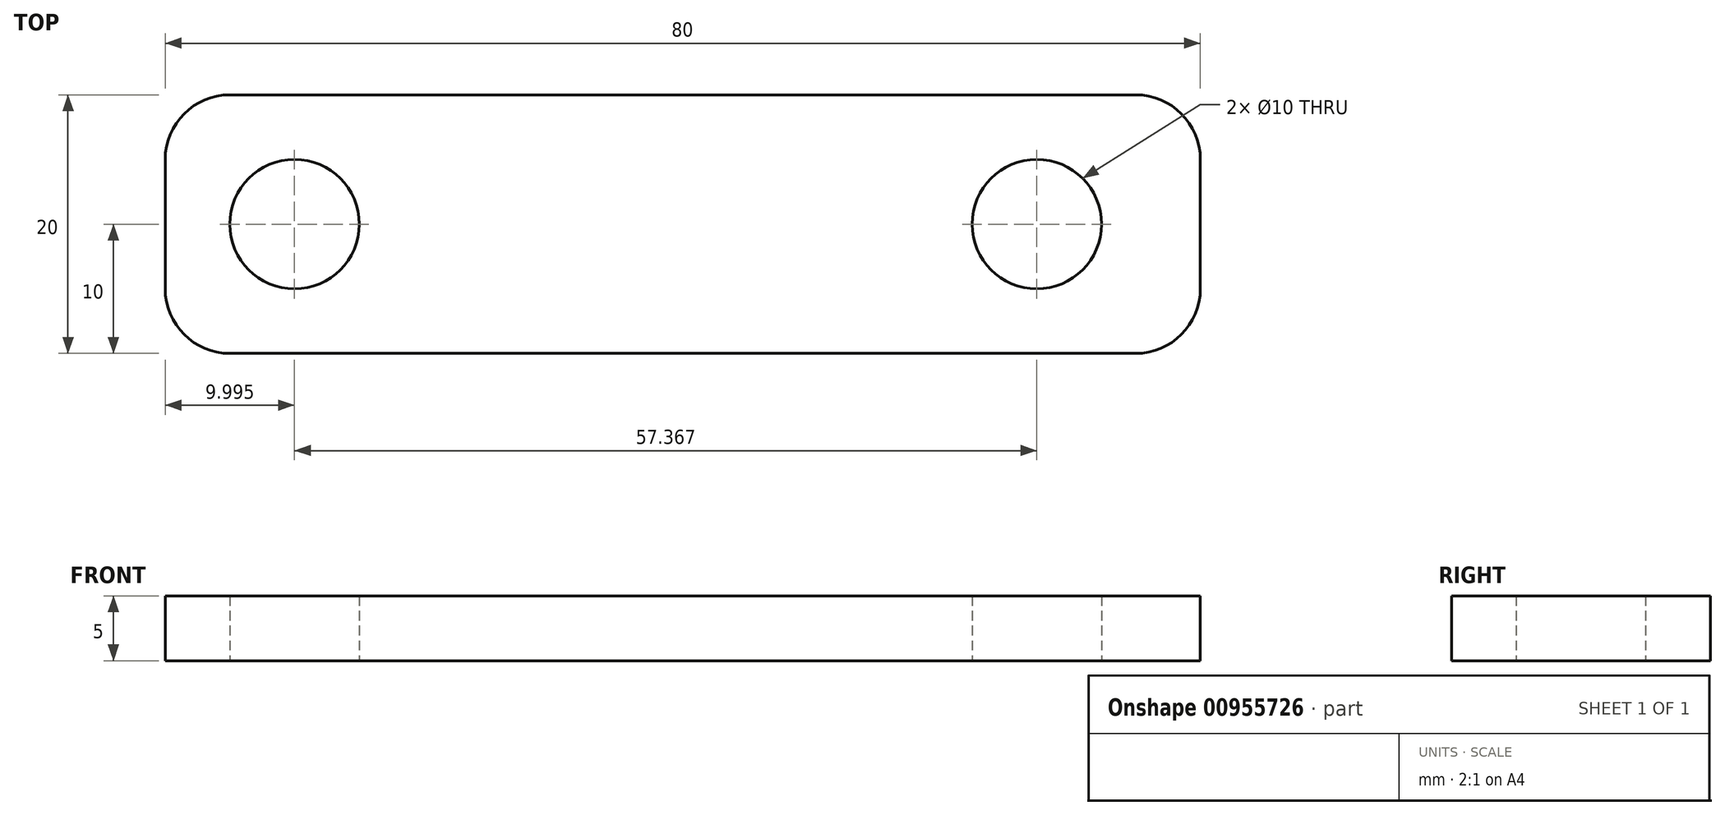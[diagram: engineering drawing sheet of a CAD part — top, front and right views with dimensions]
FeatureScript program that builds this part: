
annotation { "Feature Type Name" : "Feature", "Feature Type Description" : "" }
export const myFeature = defineFeature(function(context is Context, id is Id, definition is map)
    precondition{}
    {
        {
            var Q0;
            Q0=qCreatedBy(makeId("Top.planeOp"),FACE);
            var sketch = newSketch(context, id + "F0", { "sketchPlane" : qUnion([Q0])});
            skLineSegment(sketch, "E0.bottom", {"start": v(40, 10) * mm, "end": v(-40, 10) * mm});
            skLineSegment(sketch, "E0.top", {"start": v(40, -10) * mm, "end": v(-40, -10) * mm});
            skLineSegment(sketch, "E0.left", {"start": v(40, 10) * mm, "end": v(40, -10) * mm});
            skLineSegment(sketch, "E0.right", {"start": v(-40, 10) * mm, "end": v(-40, -10) * mm});
            skPoint(sketch, "E0.middle", {"position": v(0, 0) * mm});
            skSolve(sketch);
        }
        {
            var Q0;
            Q0=makeQuery(id+"F0.imprint","IMPRINT",FACE,{"disambiguationData":[TD([[makeQuery(id+"F0.imprint","IMPRINT",EDGE,{"derivedFrom":sQuery(id+"F0.wireOp",EDGE,"E0.bottom")}),1.0]])]});
            extrude(context, id + "F1", {"entities" : qUnion([Q0]), "depth" : 5 * mm, "offsetDistance" : 25 * mm});
        }
        {
            var Q0;
            Q0=qCreatedBy(makeId("Top.planeOp"),FACE);
            var sketch = newSketch(context, id + "F2", { "sketchPlane" : qUnion([Q0])});
            skCircle(sketch, "E1", {"center": v(-30, 0) * mm, "radius": 5 * mm});
            skCircle(sketch, "E2", {"center": v(27.36, 0) * mm, "radius": 5 * mm});
            skSolve(sketch);
        }
        {
            var Q0;
            Q0 = qSketchRegion(id + "F2", true);
            extrude(context, id + "F3", {"entities" : qUnion([Q0]), "operationType" : NewBodyOperationType.REMOVE, "endBound" : BoundingType.THROUGH_ALL, "depth" : 25 * mm, "offsetDistance" : 25 * mm});
        }
        {
            var Q0;
            Q0=makeQuery(id+"F1.opExtrude","SWEPT_EDGE",EDGE,{"disambiguationData":[OSD([sQuery(id+"F0.wireOp",EDGE,"E0.top"),sQuery(id+"F0.wireOp",EDGE,"E0.left")])]});
            var Q1;
            Q1=makeQuery(id+"F1.opExtrude","SWEPT_EDGE",EDGE,{"disambiguationData":[OSD([sQuery(id+"F0.wireOp",EDGE,"E0.bottom"),sQuery(id+"F0.wireOp",EDGE,"E0.left")])]});
            var Q2;
            Q2=makeQuery(id+"F1.opExtrude","SWEPT_EDGE",EDGE,{"disambiguationData":[OSD([sQuery(id+"F0.wireOp",EDGE,"E0.top"),sQuery(id+"F0.wireOp",EDGE,"E0.right")])]});
            var Q3;
            Q3=makeQuery(id+"F1.opExtrude","SWEPT_EDGE",EDGE,{"disambiguationData":[OSD([sQuery(id+"F0.wireOp",EDGE,"E0.bottom"),sQuery(id+"F0.wireOp",EDGE,"E0.right")])]});
            fillet(context, id + "F4", {"entities" : qUnion([Q0, Q1, Q2, Q3]), "radius" : 5 * mm, "tangentPropagation" : true, "allowEdgeOverflow" : false});
        }
    });
